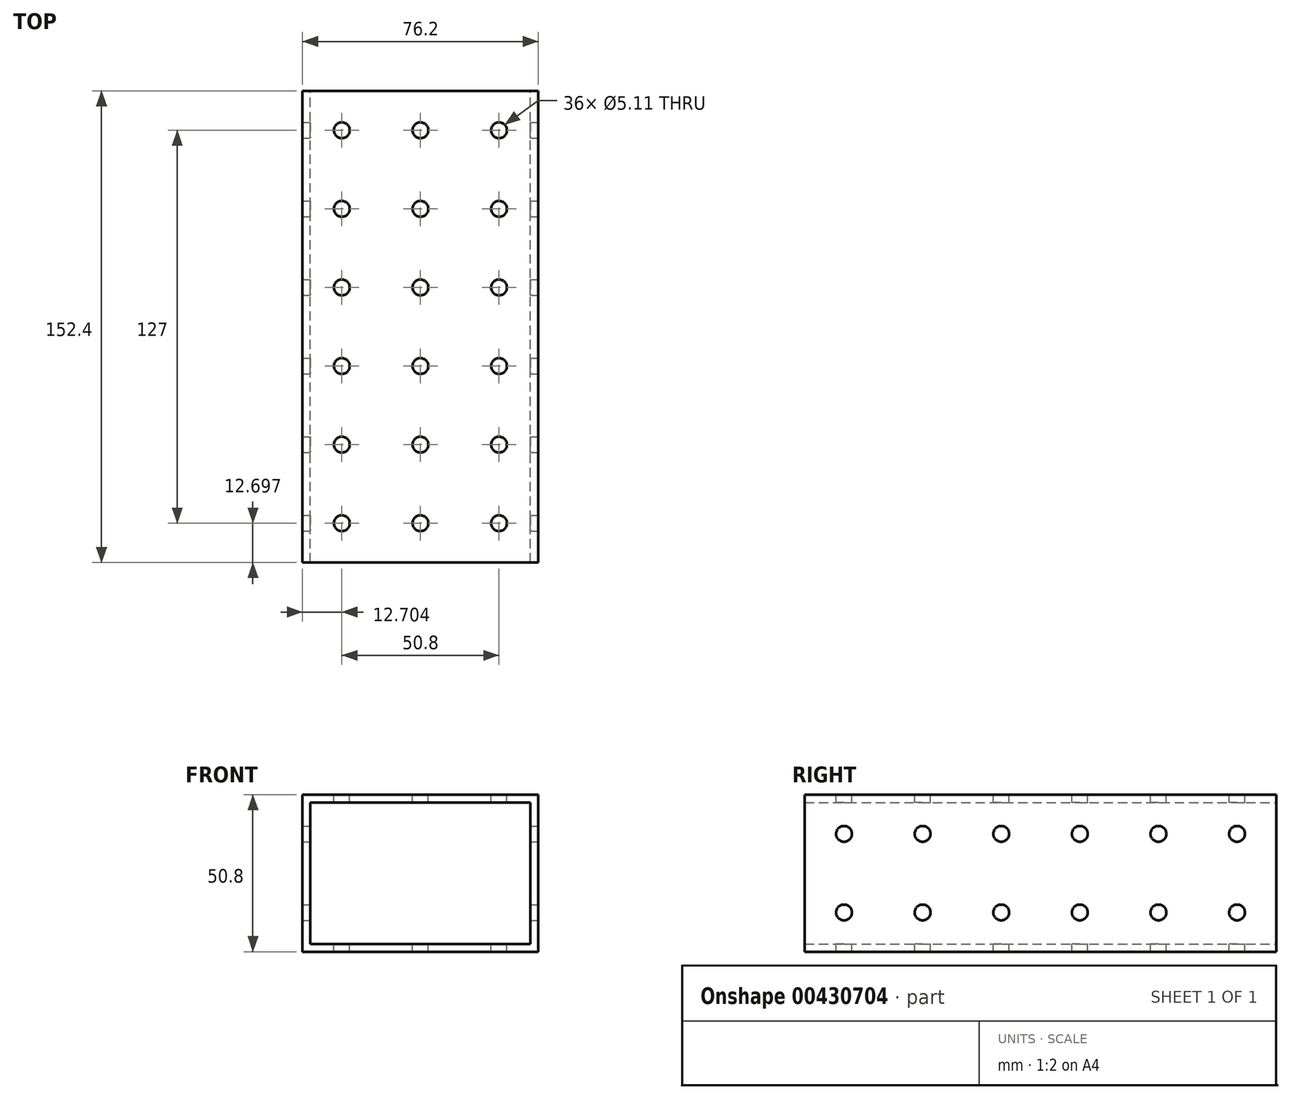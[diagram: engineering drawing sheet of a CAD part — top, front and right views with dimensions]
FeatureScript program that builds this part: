
annotation { "Feature Type Name" : "Feature", "Feature Type Description" : "" }
export const myFeature = defineFeature(function(context is Context, id is Id, definition is map)
    precondition{}
    {
        {
            var Q0;
            Q0=qCreatedBy(makeId("Top.planeOp"),FACE);
            var sketch = newSketch(context, id + "F0", { "sketchPlane" : qUnion([Q0])});
            skLineSegment(sketch, "E0.bottom", {"start": v(-34.92, 63.3) * mm, "end": v(41.28, 63.3) * mm});
            skLineSegment(sketch, "E0.top", {"start": v(-34.92, -89.1) * mm, "end": v(41.28, -89.1) * mm});
            skLineSegment(sketch, "E0.left", {"start": v(-34.92, 63.3) * mm, "end": v(-34.92, -89.1) * mm});
            skLineSegment(sketch, "E0.right", {"start": v(41.28, 63.3) * mm, "end": v(41.28, -89.1) * mm});
            skSolve(sketch);
        }
        {
            var Q0;
            Q0=makeQuery(id+"F0.imprint","IMPRINT",FACE,{"disambiguationData":[TD([[makeQuery(id+"F0.imprint","IMPRINT",EDGE,{"derivedFrom":sQuery(id+"F0.wireOp",EDGE,"E0.bottom")}),-1.0]])]});
            extrude(context, id + "F1", {"entities" : qUnion([Q0]), "depth" : 50.8 * mm});
        }
        {
            var Q0;
            Q0=makeQuery(id+"F1.opExtrude","CAP_FACE",FACE,{"disambiguationData":[OSD([sQuery(id+"F0.wireOp",EDGE,"E0.bottom"),sQuery(id+"F0.wireOp",EDGE,"E0.top"),sQuery(id+"F0.wireOp",EDGE,"E0.left"),sQuery(id+"F0.wireOp",EDGE,"E0.right")])],"isStart":false});
            var sketch = newSketch(context, id + "F2", { "sketchPlane" : qUnion([Q0])});
            skCircle(sketch, "E1", {"center": v(-22.22, 50.6) * mm, "radius": 2.55 * mm});
            skCircle(sketch, "E2.0.1.0", {"center": v(-22.22, 25.2) * mm, "radius": 2.55 * mm});
            skCircle(sketch, "E2.0.2.0", {"center": v(-22.22, -0.2) * mm, "radius": 2.55 * mm});
            skCircle(sketch, "E2.0.3.0", {"center": v(-22.22, -25.6) * mm, "radius": 2.55 * mm});
            skCircle(sketch, "E2.0.4.0", {"center": v(-22.22, -51) * mm, "radius": 2.55 * mm});
            skCircle(sketch, "E2.0.5.0", {"center": v(-22.22, -76.4) * mm, "radius": 2.55 * mm});
            skCircle(sketch, "E2.1.0.0", {"center": v(3.18, 50.6) * mm, "radius": 2.55 * mm});
            skCircle(sketch, "E2.1.1.0", {"center": v(3.18, 25.2) * mm, "radius": 2.55 * mm});
            skCircle(sketch, "E2.1.2.0", {"center": v(3.18, -0.2) * mm, "radius": 2.55 * mm});
            skCircle(sketch, "E2.1.3.0", {"center": v(3.18, -25.6) * mm, "radius": 2.55 * mm});
            skCircle(sketch, "E2.1.4.0", {"center": v(3.18, -51) * mm, "radius": 2.55 * mm});
            skCircle(sketch, "E2.1.5.0", {"center": v(3.18, -76.4) * mm, "radius": 2.55 * mm});
            skCircle(sketch, "E2.2.0.0", {"center": v(28.58, 50.6) * mm, "radius": 2.55 * mm});
            skCircle(sketch, "E2.2.1.0", {"center": v(28.58, 25.2) * mm, "radius": 2.55 * mm});
            skCircle(sketch, "E2.2.2.0", {"center": v(28.58, -0.2) * mm, "radius": 2.55 * mm});
            skCircle(sketch, "E2.2.3.0", {"center": v(28.58, -25.6) * mm, "radius": 2.55 * mm});
            skCircle(sketch, "E2.2.4.0", {"center": v(28.58, -51) * mm, "radius": 2.55 * mm});
            skCircle(sketch, "E2.2.5.0", {"center": v(28.58, -76.4) * mm, "radius": 2.55 * mm});
            skLineSegment(sketch, "E2.direction1", {"start": v(-22.22, 50.6) * mm, "end": v(3.18, 50.6) * mm, "construction": true});
            skLineSegment(sketch, "E2.direction2", {"start": v(-22.22, 50.6) * mm, "end": v(-22.22, 25.2) * mm, "construction": true});
            skSolve(sketch);
        }
        {
            var Q0;
            Q0=sQuery(id+"F2.wireOp",VERTEX,"E2.0.2.0.center");
            var Q1;
            Q1=sQuery(id+"F2.wireOp",VERTEX,"E2.2.2.0.center");
            var Q2;
            Q2=sQuery(id+"F2.wireOp",VERTEX,"E2.1.4.0.center");
            var Q3;
            Q3=sQuery(id+"F2.wireOp",VERTEX,"E2.1.3.0.center");
            var Q4;
            Q4=sQuery(id+"F2.wireOp",VERTEX,"E2.2.4.0.center");
            var Q5;
            Q5=sQuery(id+"F2.wireOp",VERTEX,"E2.2.3.0.center");
            var Q6;
            Q6=sQuery(id+"F2.wireOp",VERTEX,"E2.2.1.0.center");
            var Q7;
            Q7=sQuery(id+"F2.wireOp",VERTEX,"E2.2.5.0.center");
            var Q8;
            Q8=sQuery(id+"F2.wireOp",VERTEX,"E2.direction1.end");
            var Q9;
            Q9=sQuery(id+"F2.wireOp",VERTEX,"E2.1.5.0.center");
            var Q10;
            Q10=sQuery(id+"F2.wireOp",VERTEX,"E2.2.0.0.center");
            var Q11;
            Q11=sQuery(id+"F2.wireOp",VERTEX,"E2.1.2.0.center");
            var Q12;
            Q12=sQuery(id+"F2.wireOp",VERTEX,"E2.1.1.0.center");
            var Q13;
            Q13=sQuery(id+"F2.wireOp",VERTEX,"E2.0.1.0.center");
            var Q14;
            Q14=sQuery(id+"F2.wireOp",VERTEX,"E2.0.5.0.center");
            var Q15;
            Q15=sQuery(id+"F2.wireOp",VERTEX,"E1.center");
            var Q16;
            Q16=sQuery(id+"F2.wireOp",VERTEX,"E2.0.3.0.center");
            var Q17;
            Q17=sQuery(id+"F2.wireOp",VERTEX,"E2.0.4.0.center");
            var Q18;
            Q18=makeQuery(id+"F1.opExtrude","SWEPT_BODY",BODY,{"disambiguationData":[OSD([sQuery(id+"F0.wireOp",EDGE,"E0.bottom"),sQuery(id+"F0.wireOp",EDGE,"E0.top"),sQuery(id+"F0.wireOp",EDGE,"E0.left"),sQuery(id+"F0.wireOp",EDGE,"E0.right")])]});
            hole(context, id + "F3", {"style" : HoleStyle.SIMPLE, "endStyle" : HoleEndStyle.THROUGH, "holeDiameter" : 5.1 * mm, "isTappedThrough" : true, "tappedDepth" : 12.7 * mm, "tapClearance" : 3, "locations" : qUnion([Q0, Q1, Q2, Q3, Q4, Q5, Q6, Q7, Q8, Q9, Q10, Q11, Q12, Q13, Q14, Q15, Q16, Q17]), "scope" : qUnion([Q18])});
        }
        {
            var Q0;
            Q0=makeQuery(id+"F1.opExtrude","SWEPT_FACE",FACE,{"disambiguationData":[OSD([sQuery(id+"F0.wireOp",EDGE,"E0.right")])]});
            var sketch = newSketch(context, id + "F4", { "sketchPlane" : qUnion([Q0])});
            skCircle(sketch, "E3", {"center": v(50.6, 38.1) * mm, "radius": 2.55 * mm});
            skCircle(sketch, "E4.0.1.0", {"center": v(50.6, 12.7) * mm, "radius": 2.55 * mm});
            skCircle(sketch, "E4.1.0.0", {"center": v(25.2, 38.1) * mm, "radius": 2.55 * mm});
            skCircle(sketch, "E4.1.1.0", {"center": v(25.2, 12.7) * mm, "radius": 2.55 * mm});
            skCircle(sketch, "E4.2.0.0", {"center": v(-0.2, 38.1) * mm, "radius": 2.55 * mm});
            skCircle(sketch, "E4.2.1.0", {"center": v(-0.2, 12.7) * mm, "radius": 2.55 * mm});
            skCircle(sketch, "E4.3.0.0", {"center": v(-25.6, 38.1) * mm, "radius": 2.55 * mm});
            skCircle(sketch, "E4.3.1.0", {"center": v(-25.6, 12.7) * mm, "radius": 2.55 * mm});
            skCircle(sketch, "E4.4.0.0", {"center": v(-51, 38.1) * mm, "radius": 2.55 * mm});
            skCircle(sketch, "E4.4.1.0", {"center": v(-51, 12.7) * mm, "radius": 2.55 * mm});
            skCircle(sketch, "E4.5.0.0", {"center": v(-76.4, 38.1) * mm, "radius": 2.55 * mm});
            skCircle(sketch, "E4.5.1.0", {"center": v(-76.4, 12.7) * mm, "radius": 2.55 * mm});
            skLineSegment(sketch, "E4.direction1", {"start": v(50.6, 38.1) * mm, "end": v(25.2, 38.1) * mm, "construction": true});
            skLineSegment(sketch, "E4.direction2", {"start": v(50.6, 38.1) * mm, "end": v(50.6, 12.7) * mm, "construction": true});
            skSolve(sketch);
        }
        {
            var Q0;
            Q0=sQuery(id+"F4.wireOp",VERTEX,"E4.3.0.0.center");
            var Q1;
            Q1=sQuery(id+"F4.wireOp",VERTEX,"E4.2.1.0.center");
            var Q2;
            Q2=sQuery(id+"F4.wireOp",VERTEX,"E4.4.0.0.center");
            var Q3;
            Q3=sQuery(id+"F4.wireOp",VERTEX,"E4.3.1.0.center");
            var Q4;
            Q4=sQuery(id+"F4.wireOp",VERTEX,"E4.0.1.0.center");
            var Q5;
            Q5=sQuery(id+"F4.wireOp",VERTEX,"E3.center");
            var Q6;
            Q6=sQuery(id+"F4.wireOp",VERTEX,"E4.2.0.0.center");
            var Q7;
            Q7=sQuery(id+"F4.wireOp",VERTEX,"E4.1.1.0.center");
            var Q8;
            Q8=sQuery(id+"F4.wireOp",VERTEX,"E4.4.1.0.center");
            var Q9;
            Q9=sQuery(id+"F4.wireOp",VERTEX,"E4.5.1.0.center");
            var Q10;
            Q10=sQuery(id+"F4.wireOp",VERTEX,"E4.5.0.0.center");
            var Q11;
            Q11=sQuery(id+"F4.wireOp",VERTEX,"E4.direction1.end");
            var Q12;
            Q12=makeQuery(id+"F1.opExtrude","SWEPT_BODY",BODY,{"disambiguationData":[OSD([sQuery(id+"F0.wireOp",EDGE,"E0.bottom"),sQuery(id+"F0.wireOp",EDGE,"E0.top"),sQuery(id+"F0.wireOp",EDGE,"E0.left"),sQuery(id+"F0.wireOp",EDGE,"E0.right")])]});
            hole(context, id + "F5", {"style" : HoleStyle.SIMPLE, "endStyle" : HoleEndStyle.THROUGH, "holeDiameter" : 5.1 * mm, "isTappedThrough" : true, "tappedDepth" : 12.7 * mm, "tapClearance" : 3, "locations" : qUnion([Q0, Q1, Q2, Q3, Q4, Q5, Q6, Q7, Q8, Q9, Q10, Q11]), "scope" : qUnion([Q12])});
        }
        {
            var Q0;
            Q0=makeQuery(id+"F1.opExtrude","SWEPT_FACE",FACE,{"disambiguationData":[OSD([sQuery(id+"F0.wireOp",EDGE,"E0.bottom")])]});
            var sketch = newSketch(context, id + "F6", { "sketchPlane" : qUnion([Q0])});
            skLineSegment(sketch, "E5.bottom", {"start": v(-38.74, 48.26) * mm, "end": v(32.38, 48.26) * mm});
            skLineSegment(sketch, "E5.top", {"start": v(-38.74, 2.54) * mm, "end": v(32.38, 2.54) * mm});
            skLineSegment(sketch, "E5.left", {"start": v(-38.74, 48.26) * mm, "end": v(-38.74, 2.54) * mm});
            skLineSegment(sketch, "E5.right", {"start": v(32.38, 48.26) * mm, "end": v(32.38, 2.54) * mm});
            skSolve(sketch);
        }
        {
            var Q0;
            Q0=makeQuery(id+"F6.imprint","IMPRINT",FACE,{"disambiguationData":[TD([[makeQuery(id+"F6.imprint","IMPRINT",EDGE,{"derivedFrom":sQuery(id+"F6.wireOp",EDGE,"E5.bottom")}),-1.0]])]});
            extrude(context, id + "F7", {"entities" : qUnion([Q0]), "operationType" : NewBodyOperationType.REMOVE, "oppositeDirection" : true, "depth" : 152.4 * mm});
        }
    });
